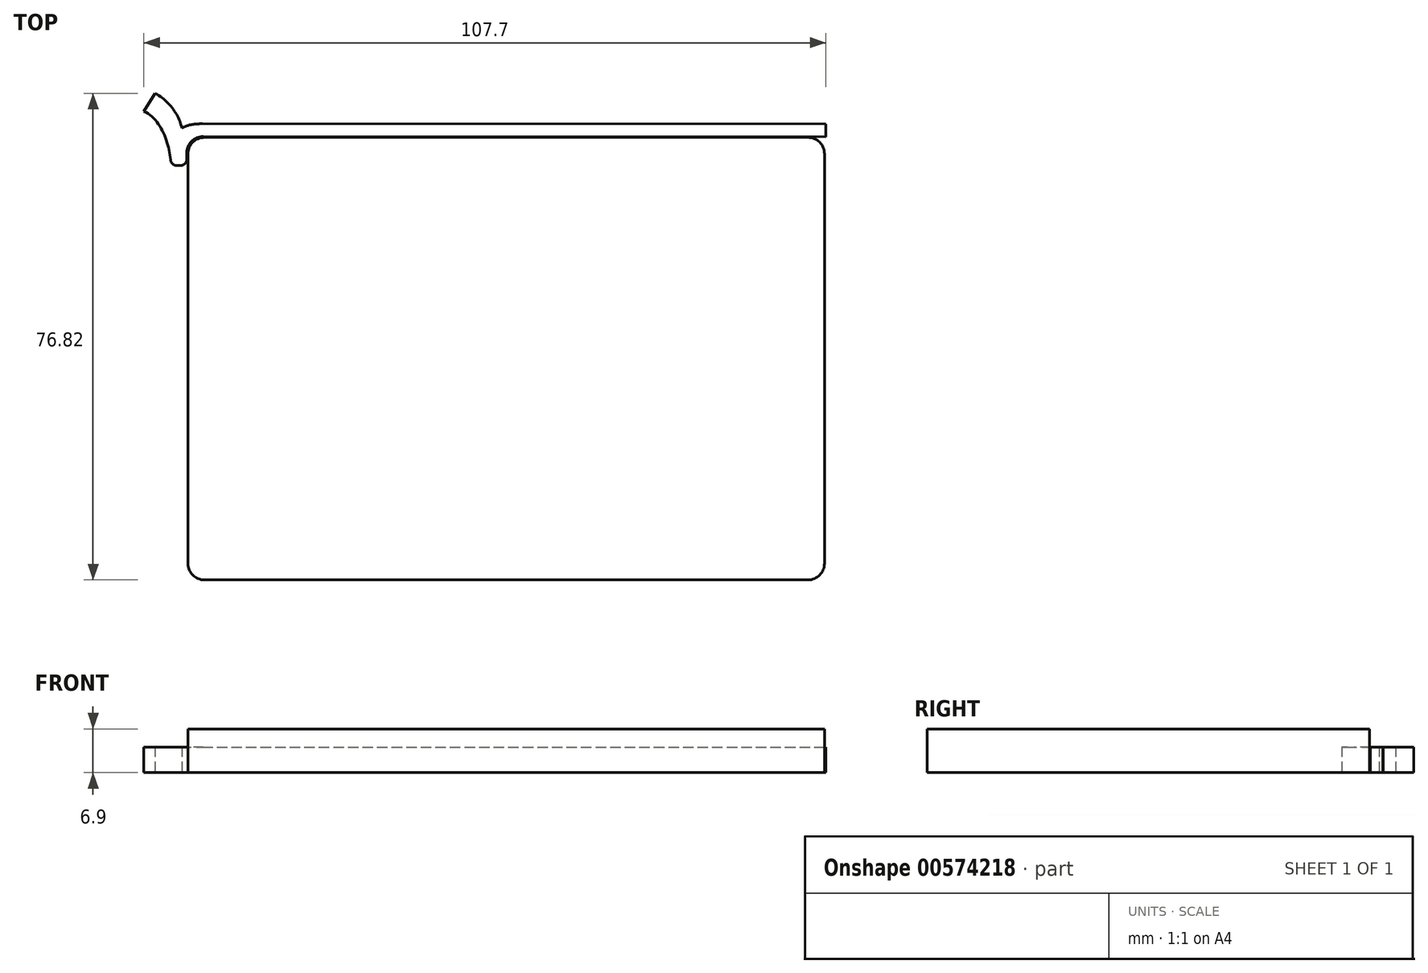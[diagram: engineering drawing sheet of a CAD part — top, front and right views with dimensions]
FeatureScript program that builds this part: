
annotation { "Feature Type Name" : "Feature", "Feature Type Description" : "" }
export const myFeature = defineFeature(function(context is Context, id is Id, definition is map)
    precondition{}
    {
        {
            var Q0;
            Q0=qCreatedBy(makeId("Top.planeOp"),FACE);
            var sketch = newSketch(context, id + "F0", { "sketchPlane" : qUnion([Q0])});
            skLineSegment(sketch, "E0.bottom", {"start": v(-50.25, -34.92) * mm, "end": v(50.25, -34.92) * mm});
            skLineSegment(sketch, "E0.top", {"start": v(-50.25, 34.92) * mm, "end": v(50.25, 34.92) * mm});
            skLineSegment(sketch, "E0.left", {"start": v(-50.25, -34.92) * mm, "end": v(-50.25, 34.92) * mm});
            skLineSegment(sketch, "E0.right", {"start": v(50.25, -34.92) * mm, "end": v(50.25, 34.92) * mm});
            skPoint(sketch, "E0.middle", {"position": v(0, 0) * mm});
            skSolve(sketch);
        }
        {
            var Q0;
            Q0 = qSketchRegion(id + "F0", true);
            extrude(context, id + "F1", {"entities" : qUnion([Q0]), "depth" : 6.9 * mm, "offsetDistance" : 25 * mm});
        }
        {
            var Q0;
            Q0=makeQuery(id+"F1.opExtrude","SWEPT_EDGE",EDGE,{"disambiguationData":[OSD([sQuery(id+"F0.wireOp",EDGE,"E0.top"),sQuery(id+"F0.wireOp",EDGE,"E0.right")])]});
            var Q1;
            Q1=makeQuery(id+"F1.opExtrude","SWEPT_EDGE",EDGE,{"disambiguationData":[OSD([sQuery(id+"F0.wireOp",EDGE,"E0.top"),sQuery(id+"F0.wireOp",EDGE,"E0.left")])]});
            var Q2;
            Q2=makeQuery(id+"F1.opExtrude","SWEPT_EDGE",EDGE,{"disambiguationData":[OSD([sQuery(id+"F0.wireOp",EDGE,"E0.bottom"),sQuery(id+"F0.wireOp",EDGE,"E0.right")])]});
            var Q3;
            Q3=makeQuery(id+"F1.opExtrude","SWEPT_EDGE",EDGE,{"disambiguationData":[OSD([sQuery(id+"F0.wireOp",EDGE,"E0.bottom"),sQuery(id+"F0.wireOp",EDGE,"E0.left")])]});
            fillet(context, id + "F2", {"entities" : qUnion([Q0, Q1, Q2, Q3]), "radius" : 2.6 * mm, "tangentPropagation" : true, "allowEdgeOverflow" : false});
        }
        {
            var Q0;
            Q0=qCreatedBy(makeId("Top.planeOp"),FACE);
            var sketch = newSketch(context, id + "F3", { "sketchPlane" : qUnion([Q0])});
            skPoint(sketch, "E1.middle", {"position": v(0, 0) * mm});
            skLineSegment(sketch, "E2", {"start": v(-51.43, 30.48) * mm, "end": v(-52, 30.48) * mm});
            skLineSegment(sketch, "E3", {"start": v(-47.99, 37.08) * mm, "end": v(50.49, 37.02) * mm});
            skLineSegment(sketch, "E4", {"start": v(-50.43, 31.48) * mm, "end": v(-50.43, 32.48) * mm});
            skLineSegment(sketch, "E5", {"start": v(-47.83, 35.08) * mm, "end": v(50.46, 35.02) * mm});
            skArc(sketch, "E6.filletArc", {"start": v(-47.83, 35.08) * mm, "mid": v(-49.67, 34.32) * mm, "end": v(-50.43, 32.48) * mm});
            skFitSpline(sketch, "E7", {"points": [v(-52.93, 30.48) * mm, v(-57.2, 39.04) * mm], "startDerivative": vector(-0.2, 8.36) * mm, "endDerivative": vector(-8.9, 3.85) * mm});
            skPoint(sketch, "E8.visualSharp", {"position": v(-50.43, 30.48) * mm});
            skArc(sketch, "E8.filletArc", {"start": v(-51.43, 30.48) * mm, "mid": v(-50.73, 30.78) * mm, "end": v(-50.43, 31.48) * mm});
            skArc(sketch, "E9.filletArc", {"start": v(-53, 31.38) * mm, "mid": v(-52.67, 30.74) * mm, "end": v(-52, 30.48) * mm});
            skLineSegment(sketch, "E10", {"start": v(-57.2, 39.04) * mm, "end": v(-55.45, 41.89) * mm});
            skFitSpline(sketch, "E11", {"points": [v(-55.45, 41.89) * mm, v(-51.22, 36.4) * mm], "startDerivative": vector(6.85, -3.75) * mm, "endDerivative": vector(1.34, -6.3) * mm});
            skFitSpline(sketch, "E12", {"points": [v(-51.22, 36.4) * mm, v(-47.99, 37.08) * mm], "startDerivative": vector(2.93, 1.48) * mm, "endDerivative": vector(4.68, 0) * mm});
            skLineSegment(sketch, "E13", {"start": v(50.49, 37.02) * mm, "end": v(50.46, 35.02) * mm});
            skSolve(sketch);
        }
        {
            var Q0;
            Q0 = qSketchRegion(id + "F3", true);
            extrude(context, id + "F4", {"entities" : qUnion([Q0]), "depth" : 4 * mm, "offsetDistance" : 25 * mm});
        }
    });
